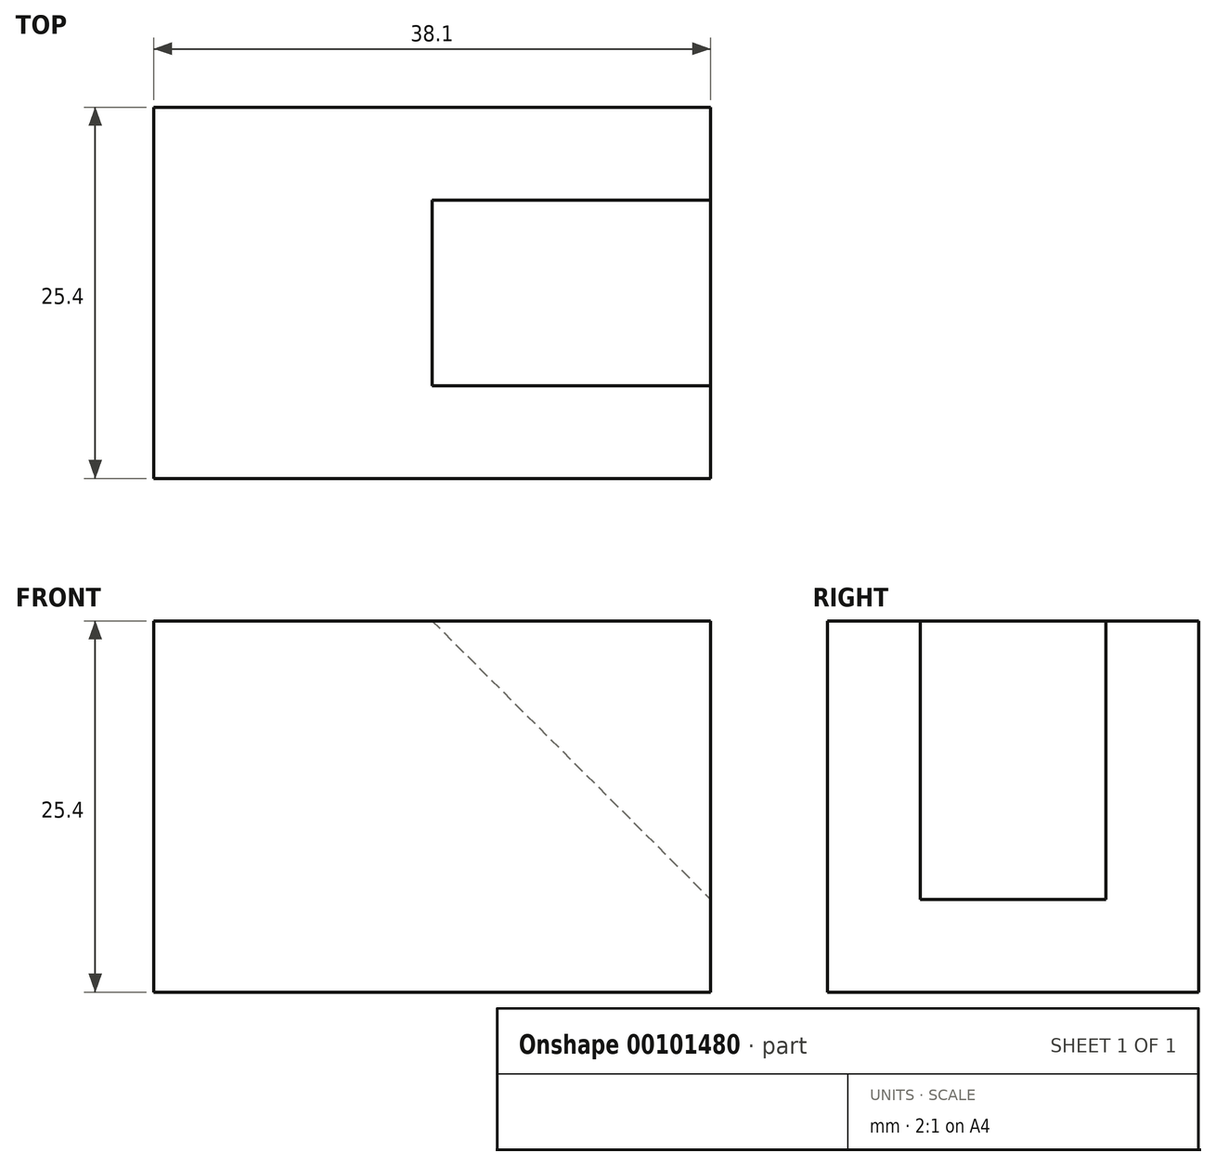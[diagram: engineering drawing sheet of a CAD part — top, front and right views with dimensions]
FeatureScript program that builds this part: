
annotation { "Feature Type Name" : "Feature", "Feature Type Description" : "" }
export const myFeature = defineFeature(function(context is Context, id is Id, definition is map)
    precondition{}
    {
        {
            var Q0;
            Q0=qCreatedBy(makeId("Front.planeOp"),FACE);
            var sketch = newSketch(context, id + "F0", { "sketchPlane" : qUnion([Q0])});
            skLineSegment(sketch, "E0", {"start": v(0, 0) * mm, "end": v(0, 25.4) * mm});
            skLineSegment(sketch, "E1", {"start": v(0, 25.4) * mm, "end": v(38.1, 25.4) * mm});
            skLineSegment(sketch, "E2", {"start": v(38.1, 25.4) * mm, "end": v(38.1, 0) * mm});
            skLineSegment(sketch, "E3", {"start": v(38.1, 0) * mm, "end": v(0, 0) * mm});
            skSolve(sketch);
        }
        {
            var Q0;
            Q0=makeQuery(id+"F0.imprint","IMPRINT",FACE,{"disambiguationData":[TD([[makeQuery(id+"F0.imprint","IMPRINT",EDGE,{"derivedFrom":sQuery(id+"F0.wireOp",EDGE,"E0")}),-1.0]])]});
            extrude(context, id + "F1", {"entities" : qUnion([Q0]), "endBound" : BoundingType.SYMMETRIC, "depth" : 25.4 * mm});
        }
        {
            var Q0;
            Q0=qCreatedBy(makeId("Front.planeOp"),FACE);
            var sketch = newSketch(context, id + "F2", { "sketchPlane" : qUnion([Q0])});
            skLineSegment(sketch, "E4", {"start": v(38.1, 6.35) * mm, "end": v(38.1, 25.4) * mm});
            skLineSegment(sketch, "E5", {"start": v(38.1, 25.4) * mm, "end": v(19.05, 25.4) * mm});
            skLineSegment(sketch, "E6", {"start": v(19.05, 25.4) * mm, "end": v(38.1, 6.35) * mm});
            skSolve(sketch);
        }
        {
            var Q0;
            Q0 = qSketchRegion(id + "F2", true);
            extrude(context, id + "F3", {"entities" : qUnion([Q0]), "operationType" : NewBodyOperationType.REMOVE, "endBound" : BoundingType.SYMMETRIC, "oppositeDirection" : true, "depth" : 12.7 * mm});
        }
    });
